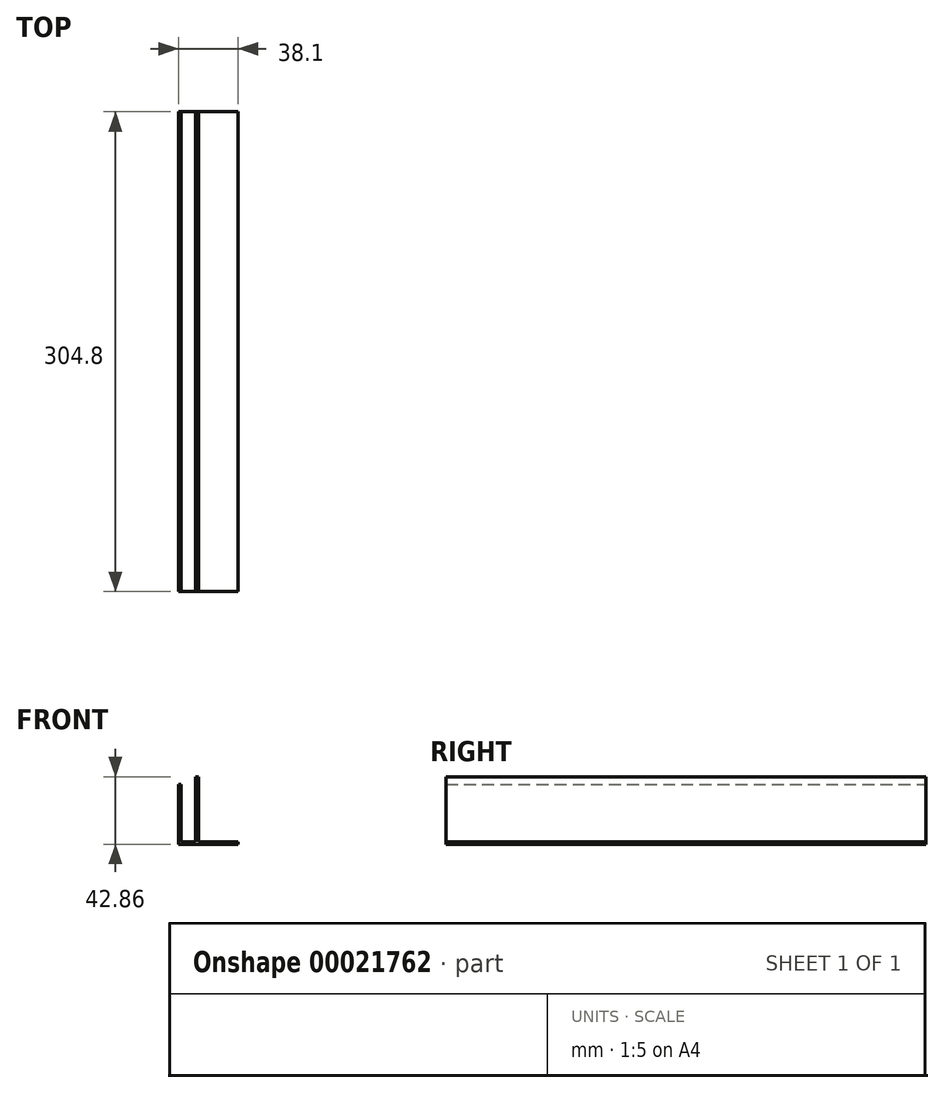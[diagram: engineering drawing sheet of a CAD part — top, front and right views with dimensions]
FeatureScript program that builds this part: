
annotation { "Feature Type Name" : "Feature", "Feature Type Description" : "" }
export const myFeature = defineFeature(function(context is Context, id is Id, definition is map)
    precondition{}
    {
        {
            var Q0;
            Q0=qCreatedBy(makeId("Front.planeOp"),FACE);
            var sketch = newSketch(context, id + "F0", { "sketchPlane" : qUnion([Q0])});
            skLineSegment(sketch, "E0", {"start": v(0, 0) * mm, "end": v(38.1, 0) * mm});
            skLineSegment(sketch, "E1", {"start": v(38.1, 0) * mm, "end": v(38.1, 1.59) * mm});
            skLineSegment(sketch, "E2", {"start": v(38.1, 1.59) * mm, "end": v(12.7, 1.59) * mm});
            skLineSegment(sketch, "E3", {"start": v(12.7, 1.59) * mm, "end": v(12.7, 42.86) * mm});
            skLineSegment(sketch, "E4", {"start": v(12.7, 42.86) * mm, "end": v(11.11, 42.86) * mm});
            skLineSegment(sketch, "E5", {"start": v(11.11, 42.86) * mm, "end": v(11.11, 1.59) * mm});
            skLineSegment(sketch, "E6", {"start": v(11.11, 1.59) * mm, "end": v(1.59, 1.59) * mm});
            skLineSegment(sketch, "E7", {"start": v(1.59, 1.59) * mm, "end": v(1.59, 38.1) * mm});
            skLineSegment(sketch, "E8", {"start": v(1.59, 38.1) * mm, "end": v(0, 38.1) * mm});
            skLineSegment(sketch, "E9", {"start": v(0, 38.1) * mm, "end": v(0, 0) * mm});
            skSolve(sketch);
        }
        {
            var Q0;
            Q0=makeQuery(id+"F0.imprint","IMPRINT",FACE,{"disambiguationData":[TD([[makeQuery(id+"F0.imprint","IMPRINT",EDGE,{"derivedFrom":sQuery(id+"F0.wireOp",EDGE,"E0")}),1.0]])]});
            extrude(context, id + "F1", {"entities" : qUnion([Q0]), "endBound" : BoundingType.SYMMETRIC, "depth" : 304.8 * mm});
        }
    });
